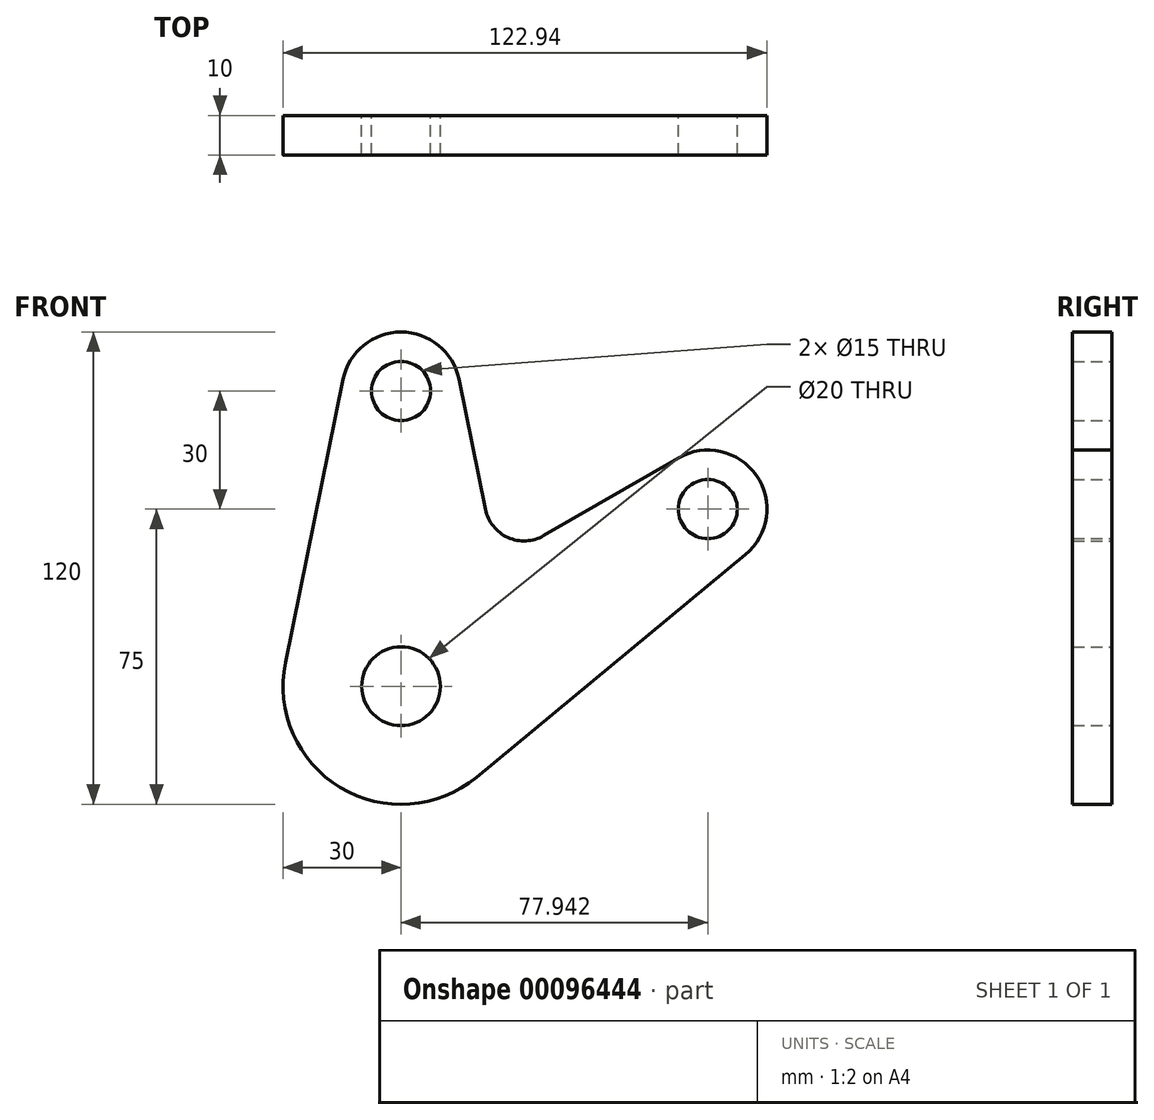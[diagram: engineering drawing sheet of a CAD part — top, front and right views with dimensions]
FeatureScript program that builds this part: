
annotation { "Feature Type Name" : "Feature", "Feature Type Description" : "" }
export const myFeature = defineFeature(function(context is Context, id is Id, definition is map)
    precondition{}
    {
        {
            var Q0;
            Q0=qCreatedBy(makeId("Front.planeOp"),FACE);
            var sketch = newSketch(context, id + "F0", { "sketchPlane" : qUnion([Q0])});
            skCircle(sketch, "E0", {"center": v(0, 0) * mm, "radius": 10 * mm});
            skCircle(sketch, "E1", {"center": v(77.94, 45) * mm, "radius": 7.5 * mm});
            skCircle(sketch, "E2", {"center": v(0, 75) * mm, "radius": 7.5 * mm});
            skLineSegment(sketch, "E3", {"start": v(0, 0) * mm, "end": v(0, 84.3) * mm, "construction": true});
            skLineSegment(sketch, "E4", {"start": v(0, 0) * mm, "end": v(77.94, 45) * mm, "construction": true});
            skArc(sketch, "E5", {"start": v(-29.4, 6) * mm, "mid": v(-15.44, -25.72) * mm, "end": v(19.12, -23.12) * mm});
            skArc(sketch, "E6", {"start": v(14.7, 78) * mm, "mid": v(0, 90) * mm, "end": v(-14.7, 78) * mm});
            skLineSegment(sketch, "E7", {"start": v(-14.7, 78) * mm, "end": v(-29.4, 6) * mm});
            skLineSegment(sketch, "E8", {"start": v(14.7, 78) * mm, "end": v(21.45, 44.9) * mm});
            skArc(sketch, "E9", {"start": v(87.5, 33.44) * mm, "mid": v(90.26, 53.56) * mm, "end": v(70.44, 58) * mm});
            skLineSegment(sketch, "E10", {"start": v(87.5, 33.44) * mm, "end": v(19.12, -23.12) * mm});
            skLineSegment(sketch, "E11", {"start": v(70.44, 58) * mm, "end": v(36.25, 38.25) * mm});
            skPoint(sketch, "E12.visualSharp", {"position": v(24.23, 31.3) * mm});
            skArc(sketch, "E12.filletArc", {"start": v(21.45, 44.9) * mm, "mid": v(27.15, 37.8) * mm, "end": v(36.25, 38.25) * mm});
            skSolve(sketch);
        }
        {
            var Q0;
            Q0 = qSketchRegion(id + "F0", true);
            extrude(context, id + "F1", {"entities" : qUnion([Q0]), "depth" : 10 * mm});
        }
    });
